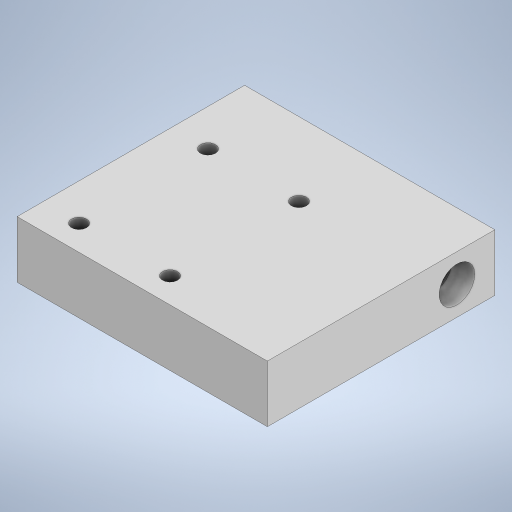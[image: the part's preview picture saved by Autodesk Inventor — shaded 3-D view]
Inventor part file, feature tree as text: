
AUTODESK INVENTOR PART (.ipt)
format: ipt  version: 2024.2 (Build 282272000, 272)  size: 235,520 bytes
history: native  units: in
note: dims shown in document units (in); Inventor stores cm internally (conversion verified against a paired STEP export)
features: extrude x4, sketch x4
ambient origin geometry x8: Origin, YZ Plane, XZ Plane, XY Plane, X Axis, Y Axis, Z Axis, Center Point
bodies: Solid1 (feature_tree)
feature tree (8):
  extrude  "Extrusion1"  Depth=1.5in
  extrude  "Extrusion2"  Depth=0.375in
  extrude  "Extrusion3"  Depth=0.25in
  extrude  "Extrusion4"  Depth=0.15in
  sketch  "Sketch1"  dims[d0=1.65in d1=1.5in]
  sketch  "Sketch2"  dims[d2=0.375in d3=0.0in d4=0.118in]
  sketch  "Sketch3"  dims[d5=0.1875in d6=0.25in]
  sketch  "Sketch4"  dims[d7=0.0in d8=0.0in d9=0.235in d10=0.15in d11=0.0in d12=0.85in d14=0.6in d16=0.1in d17=0.1in d18=0.15in d19=0.0in d20=0.1in]
